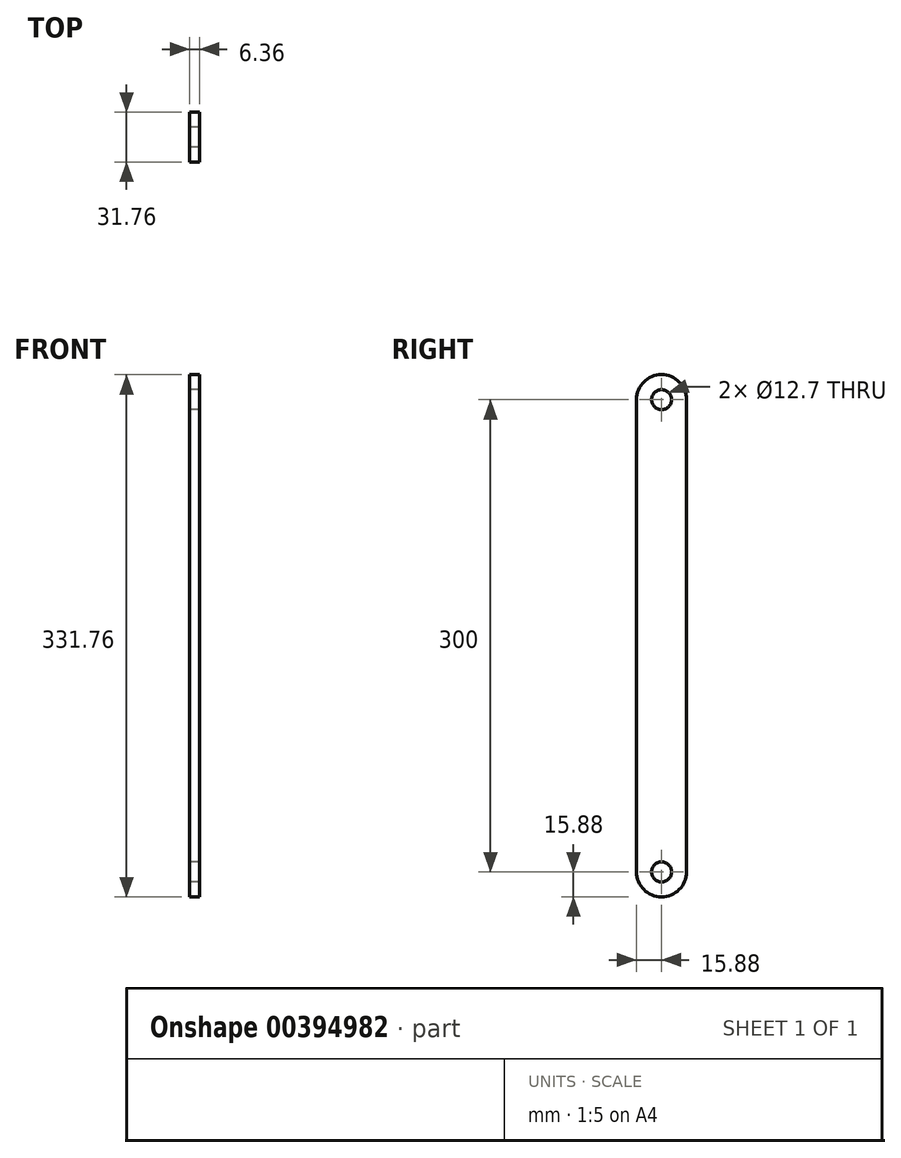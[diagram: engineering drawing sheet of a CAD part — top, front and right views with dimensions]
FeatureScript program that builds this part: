
annotation { "Feature Type Name" : "Feature", "Feature Type Description" : "" }
export const myFeature = defineFeature(function(context is Context, id is Id, definition is map)
    precondition{}
    {
        {
            var Q0;
            Q0=qCreatedBy(makeId("Right.planeOp"),FACE);
            var sketch = newSketch(context, id + "F0", { "sketchPlane" : qUnion([Q0])});
            skCircle(sketch, "E0", {"center": v(0, 0) * mm, "radius": 6.35 * mm});
            skArc(sketch, "E1", {"start": v(15.88, 0) * mm, "mid": v(0, 15.88) * mm, "end": v(-15.88, 0) * mm});
            skCircle(sketch, "E2", {"center": v(0, -300) * mm, "radius": 6.35 * mm});
            skArc(sketch, "E3", {"start": v(-15.88, -300) * mm, "mid": v(0, -315.88) * mm, "end": v(15.88, -300) * mm});
            skLineSegment(sketch, "E4", {"start": v(-15.88, 0) * mm, "end": v(-15.88, -300) * mm});
            skLineSegment(sketch, "E5", {"start": v(15.88, 0) * mm, "end": v(15.88, -300) * mm});
            skSolve(sketch);
        }
        {
            var Q0;
            Q0=qSketchRegion(id+"F0",true);
            extrude(context, id + "F1", {"entities" : qUnion([Q0]), "endBound" : BoundingType.SYMMETRIC, "depth" : 6.35 * mm});
        }
    });
